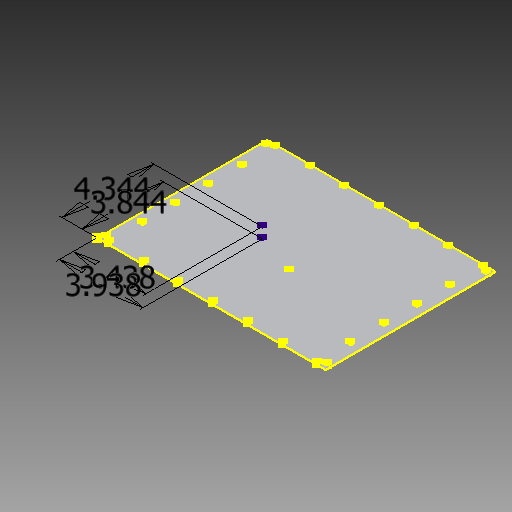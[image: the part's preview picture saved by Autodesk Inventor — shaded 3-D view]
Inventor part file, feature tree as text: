
AUTODESK INVENTOR PART (.ipt)
format: ipt  version: 2017 (Build 210142000, 142)  size: 199,168 bytes
history: native  units: in
note: dims shown in document units (in); Inventor stores cm internally (conversion verified against a paired STEP export)
features: sketch x5, hole x5, pattern_linear x5, extrude x1
ambient origin geometry x8: Origin, YZ Plane, XZ Plane, XY Plane, X Axis, Y Axis, Z Axis, Center Point
bodies: Solid1 (feature_tree)
feature tree (16):
  extrude  "Extrusion1"  Depth=10.75in
  sketch  "Sketch2"  dims[d3=0.06in d4=0.0in d7=0.0935in]
  hole  "Hole1"  [1 undecoded]
  pattern_linear  "Rectangular Pattern1"  Count1=2 Spacing1=10.375in
  hole  "Hole2"  [1 undecoded]
  pattern_linear  "Rectangular Pattern2"  Count1=7 Spacing1=1.635in
  pattern_linear  "Rectangular Pattern3"  Spacing1=0.471in  [1 undecoded]
  hole  "Hole3"  [1 undecoded]
  pattern_linear  "Rectangular Pattern4"  Count1=5 Spacing1=1.562in
  pattern_linear  "Rectangular Pattern5"  Count1=7 Spacing1=1.635in
  sketch  "Sketch3"  dims[d8=0.471in]
  sketch  "Sketch4"  dims[d9=0.1875in]
  sketch  "Sketch5"  dims[d10=0.25in d11=0.156in d12=0.75in d13=0.375in d14=0.25in d15=0.5635in d16=1.0in d17=0.8108in d18=0.7874in d20=10.375in d21=0.7874in d23=7.5in d24=0.096in d25=0.75in d26=0.16in d27=0.25in d28=0.5635in d29=1.0in d30=0.8108in d31=1.9685in d33=1.562in d34=2.7559in d36=1.635in d37=0.471in d38=0.0935in d39=0.096in d40=0.75in d41=0.16in d42=0.25in d43=0.5635in d44=1.0in d45=0.8108in d46=1.9685in d48=1.562in d49=2.7559in d51=1.635in d61=0.128in d62=0.75in d63=0.232in d64=0.25in d65=0.5635in d66=1.0in d67=0.8108in d68=0.128in d69=0.75in d70=0.232in d71=0.25in d72=0.5635in d73=1.0in d74=0.8108in d75=3.938in d76=3.438in d77=3.844in d78=4.344in]
  hole  "Hole5"  [1 undecoded]
  hole  "Hole6"  [1 undecoded]
  sketch  "Sketch1"  dims[d0=8.0in d2=10.75in]
note: 6 required parameter values undecoded (feature->parameter linkage not recoverable at this tier; creation-order binding heuristic only, values carry confidence <= 0.55)
